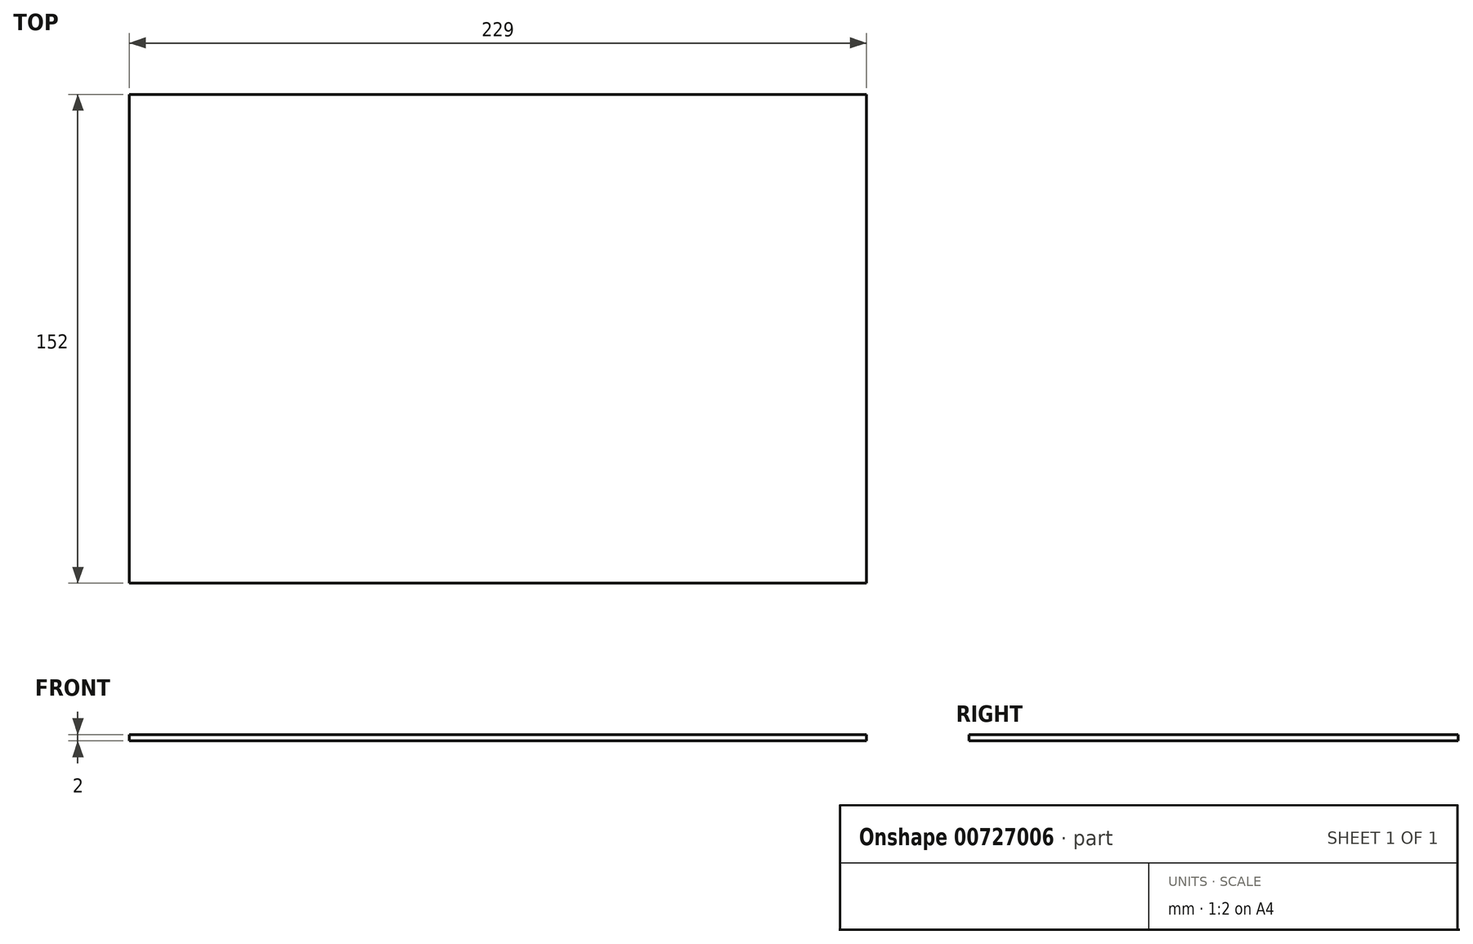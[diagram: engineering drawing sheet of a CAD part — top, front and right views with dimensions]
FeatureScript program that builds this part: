
annotation { "Feature Type Name" : "Feature", "Feature Type Description" : "" }
export const myFeature = defineFeature(function(context is Context, id is Id, definition is map)
    precondition{}
    {
        {
            var Q0;
            Q0=qCreatedBy(makeId("Top.planeOp"),FACE);
            var sketch = newSketch(context, id + "F0", { "sketchPlane" : qUnion([Q0])});
            skLineSegment(sketch, "E0.bottom", {"start": v(-99.1, 76) * mm, "end": v(129.9, 76) * mm});
            skLineSegment(sketch, "E0.top", {"start": v(-99.1, -76) * mm, "end": v(129.9, -76) * mm});
            skLineSegment(sketch, "E0.left", {"start": v(-99.1, 76) * mm, "end": v(-99.1, -76) * mm});
            skLineSegment(sketch, "E0.right", {"start": v(129.9, 76) * mm, "end": v(129.9, -76) * mm});
            skSolve(sketch);
        }
        {
            var Q0;
            Q0 = qSketchRegion(id + "F0", true);
            extrude(context, id + "F1", {"entities" : qUnion([Q0]), "depth" : 2 * mm, "offsetDistance" : 25 * mm});
        }
    });
